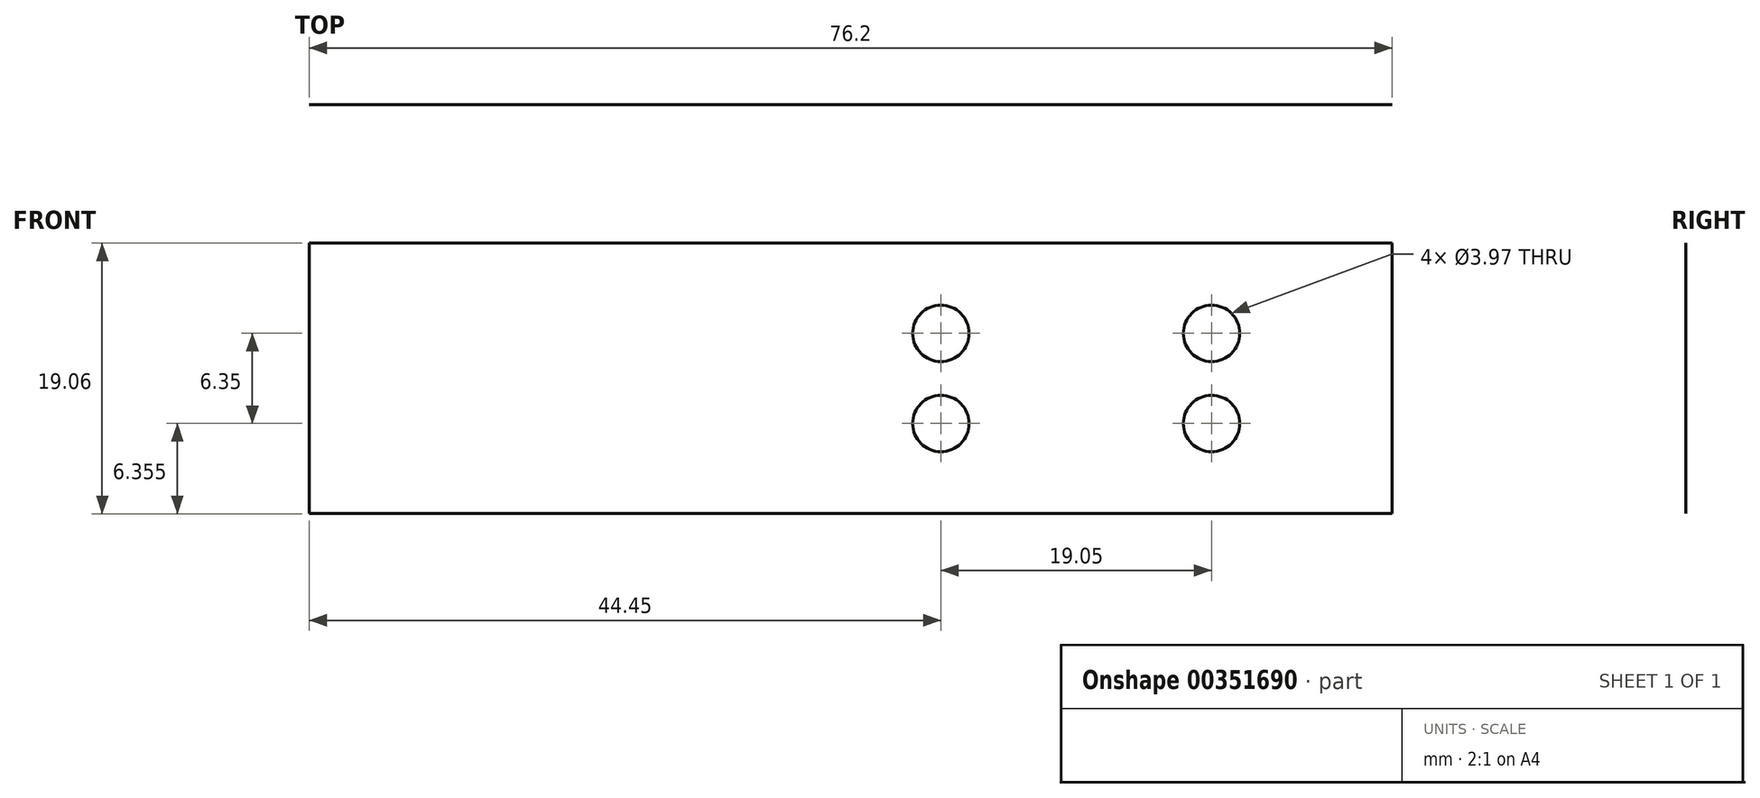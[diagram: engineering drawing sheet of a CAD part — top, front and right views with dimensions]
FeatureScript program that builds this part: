
annotation { "Feature Type Name" : "Feature", "Feature Type Description" : "" }
export const myFeature = defineFeature(function(context is Context, id is Id, definition is map)
    precondition{}
    {
        {
            var Q0;
            Q0=qCreatedBy(makeId("Front.planeOp"),FACE);
            var sketch = newSketch(context, id + "F0", { "sketchPlane" : qUnion([Q0])});
            skLineSegment(sketch, "E0.bottom", {"start": v(-38.1, 9.53) * mm, "end": v(38.1, 9.53) * mm});
            skLineSegment(sketch, "E0.top", {"start": v(-38.1, -9.53) * mm, "end": v(38.1, -9.53) * mm});
            skLineSegment(sketch, "E0.left", {"start": v(-38.1, 9.53) * mm, "end": v(-38.1, -9.53) * mm});
            skLineSegment(sketch, "E0.right", {"start": v(38.1, 9.53) * mm, "end": v(38.1, -9.53) * mm});
            skPoint(sketch, "E0.middle", {"position": v(0, 0) * mm});
            skSolve(sketch);
        }
        {
            var Q0;
            Q0 = qSketchRegion(id + "F0", true);
            extrude(context, id + "F1", {"entities" : qUnion([Q0]), "endBound" : BoundingType.SYMMETRIC, "depth" : 1 / 203.2 * mm});
        }
        {
            var Q0;
            Q0=makeQuery(id+"F1.opExtrude","CAP_FACE",FACE,{"disambiguationData":[OSD([sQuery(id+"F0.wireOp",EDGE,"E0.bottom"),sQuery(id+"F0.wireOp",EDGE,"E0.top"),sQuery(id+"F0.wireOp",EDGE,"E0.left"),sQuery(id+"F0.wireOp",EDGE,"E0.right")])],"isStart":false});
            var sketch = newSketch(context, id + "F2", { "sketchPlane" : qUnion([Q0])});
            skCircle(sketch, "E1", {"center": v(25.4, 3.18) * mm, "radius": 1.98 * mm});
            skSolve(sketch);
        }
        {
            var Q0;
            Q0=makeQuery(id+"F2.imprint","IMPRINT",FACE,{"disambiguationData":[TD([[makeQuery(id+"F2.imprint","IMPRINT",EDGE,{"derivedFrom":sQuery(id+"F2.wireOp",EDGE,"E1")}),-1.0]])]});
            var sketch = newSketch(context, id + "F3", { "sketchPlane" : qUnion([Q0])});
            skCircle(sketch, "E2", {"center": v(25.4, -3.18) * mm, "radius": 1.98 * mm});
            skSolve(sketch);
        }
        {
            var Q0;
            Q0=makeQuery(id+"F2.imprint","IMPRINT",FACE,{"disambiguationData":[TD([[makeQuery(id+"F2.imprint","IMPRINT",EDGE,{"derivedFrom":sQuery(id+"F2.wireOp",EDGE,"E1")}),-1.0]])]});
            var sketch = newSketch(context, id + "F4", { "sketchPlane" : qUnion([Q0])});
            skCircle(sketch, "E3", {"center": v(6.35, -3.17) * mm, "radius": 1.98 * mm});
            skSolve(sketch);
        }
        {
            var Q0;
            Q0=makeQuery(id+"F1.opExtrude","CAP_FACE",FACE,{"disambiguationData":[OSD([sQuery(id+"F0.wireOp",EDGE,"E0.bottom"),sQuery(id+"F0.wireOp",EDGE,"E0.top"),sQuery(id+"F0.wireOp",EDGE,"E0.left"),sQuery(id+"F0.wireOp",EDGE,"E0.right")])],"isStart":false});
            var sketch = newSketch(context, id + "F5", { "sketchPlane" : qUnion([Q0])});
            skCircle(sketch, "E4", {"center": v(6.35, 3.18) * mm, "radius": 1.98 * mm});
            skSolve(sketch);
        }
        {
            var Q0;
            Q0=makeQuery(id+"F4.imprint","IMPRINT",FACE,{"disambiguationData":[TD([[makeQuery(id+"F4.imprint","IMPRINT",EDGE,{"derivedFrom":sQuery(id+"F4.wireOp",EDGE,"E3")}),1.0]])]});
            var Q1;
            Q1 = qSketchRegion(id + "F2", true);
            var Q2;
            Q2 = qSketchRegion(id + "F3", true);
            var Q3;
            Q3 = qSketchRegion(id + "F5", true);
            var Q4;
            Q4=sQuery(id+"F4.wireOp",EDGE,"E3");
            var Q5;
            Q5=sQuery(id+"F2.wireOp",EDGE,"E1");
            var Q6;
            Q6=sQuery(id+"F3.wireOp",EDGE,"E2");
            var Q7;
            Q7=makeQuery(id+"F1.opExtrude","CAP_FACE",FACE,{"disambiguationData":[OSD([sQuery(id+"F0.wireOp",EDGE,"E0.bottom"),sQuery(id+"F0.wireOp",EDGE,"E0.top"),sQuery(id+"F0.wireOp",EDGE,"E0.left"),sQuery(id+"F0.wireOp",EDGE,"E0.right")])],"isStart":true});
            extrude(context, id + "F6", {"entities" : qUnion([Q0, Q1, Q2, Q3]), "operationType" : NewBodyOperationType.REMOVE, "surfaceEntities" : qUnion([Q4, Q5, Q6]), "endBound" : BoundingType.UP_TO_SURFACE, "oppositeDirection" : true, "endBoundEntityFace" : qUnion([Q7]), "depth" : 25.4 * mm});
        }
    });
